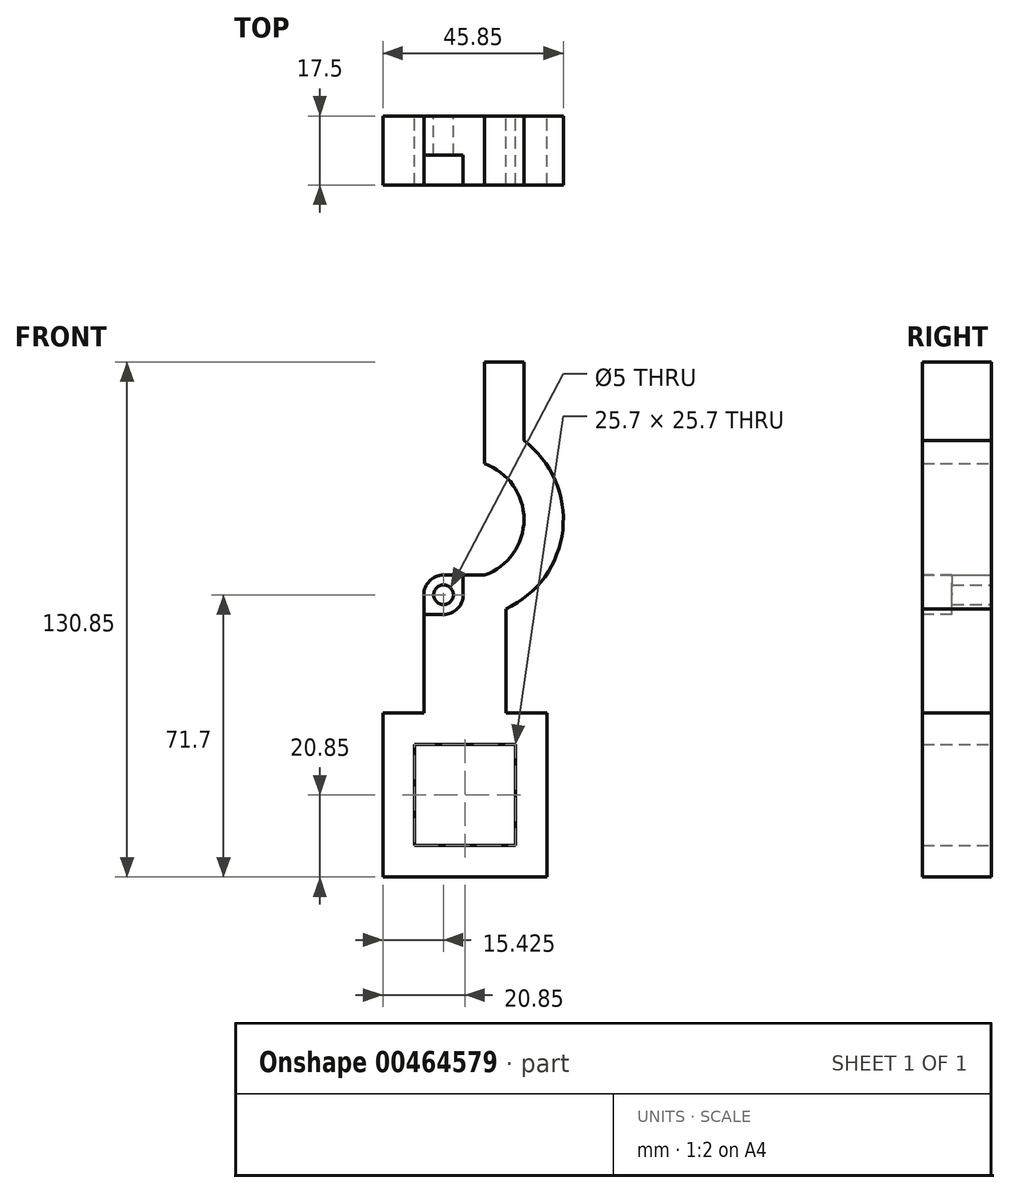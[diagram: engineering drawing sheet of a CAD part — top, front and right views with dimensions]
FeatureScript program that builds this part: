
annotation { "Feature Type Name" : "Feature", "Feature Type Description" : "" }
export const myFeature = defineFeature(function(context is Context, id is Id, definition is map)
    precondition{}
    {
        {
            var Q0;
            Q0=qCreatedBy(makeId("Front.planeOp"),FACE);
            var sketch = newSketch(context, id + "F0", { "sketchPlane" : qUnion([Q0])});
            skLineSegment(sketch, "E0", {"start": v(0, 0) * mm, "end": v(0, 12.85) * mm, "construction": true});
            skLineSegment(sketch, "E1", {"start": v(0, 12.85) * mm, "end": v(12.85, 12.85) * mm});
            skLineSegment(sketch, "E2", {"start": v(12.85, 12.85) * mm, "end": v(12.85, 0) * mm});
            skLineSegment(sketch, "E3", {"start": v(12.85, 0) * mm, "end": v(0, 0) * mm, "construction": true});
            skLineSegment(sketch, "E4", {"start": v(12.85, 0) * mm, "end": v(12.85, -12.85) * mm});
            skLineSegment(sketch, "E5", {"start": v(12.85, -12.85) * mm, "end": v(0, -12.85) * mm});
            skLineSegment(sketch, "E6", {"start": v(0, -12.85) * mm, "end": v(0, 0) * mm, "construction": true});
            skLineSegment(sketch, "E7", {"start": v(0, 0) * mm, "end": v(-12.85, 0) * mm, "construction": true});
            skLineSegment(sketch, "E8", {"start": v(-12.85, 0) * mm, "end": v(-12.85, 12.85) * mm});
            skLineSegment(sketch, "E9", {"start": v(-12.85, 12.85) * mm, "end": v(0, 12.85) * mm});
            skLineSegment(sketch, "E10", {"start": v(-12.85, 0) * mm, "end": v(-12.85, -12.85) * mm});
            skLineSegment(sketch, "E11", {"start": v(-12.85, -12.85) * mm, "end": v(0, -12.85) * mm});
            skLineSegment(sketch, "E12", {"start": v(-12.85, 0) * mm, "end": v(-20.85, 0) * mm, "construction": true});
            skLineSegment(sketch, "E13", {"start": v(-20.85, 0) * mm, "end": v(-20.85, -20.85) * mm});
            skLineSegment(sketch, "E14", {"start": v(20.85, -20.85) * mm, "end": v(20.85, 0) * mm});
            skLineSegment(sketch, "E15", {"start": v(20.85, 0) * mm, "end": v(12.85, 0) * mm, "construction": true});
            skLineSegment(sketch, "E16", {"start": v(20.85, 0) * mm, "end": v(20.85, 20.85) * mm});
            skLineSegment(sketch, "E17", {"start": v(20.85, 20.85) * mm, "end": v(10.43, 20.85) * mm});
            skLineSegment(sketch, "E18", {"start": v(-20.85, 20.85) * mm, "end": v(-20.85, 0) * mm});
            skLineSegment(sketch, "E19", {"start": v(0, 20.85) * mm, "end": v(0, 12.85) * mm, "construction": true});
            skLineSegment(sketch, "E20", {"start": v(-20.85, -20.85) * mm, "end": v(0, -20.85) * mm});
            skLineSegment(sketch, "E21", {"start": v(0, -20.85) * mm, "end": v(20.85, -20.85) * mm});
            skLineSegment(sketch, "E22", {"start": v(0, -12.85) * mm, "end": v(0, -20.85) * mm, "construction": true});
            skLineSegment(sketch, "E23", {"start": v(10.43, 20.85) * mm, "end": v(10.43, 47.28) * mm});
            skLineSegment(sketch, "E24", {"start": v(-10.43, 20.85) * mm, "end": v(-10.43, 55.85) * mm});
            skLineSegment(sketch, "E25", {"start": v(-10.43, 55.85) * mm, "end": v(4.98, 55.85) * mm});
            skArc(sketch, "E26", {"start": v(10.43, 47.28) * mm, "mid": v(24.86, 67.34) * mm, "end": v(15, 90) * mm});
            skArc(sketch, "E27", {"start": v(4.98, 55.85) * mm, "mid": v(15, 69.99) * mm, "end": v(5, 84.14) * mm});
            skLineSegment(sketch, "E28", {"start": v(0, 70) * mm, "end": v(0, 110) * mm, "construction": true});
            skLineSegment(sketch, "E29", {"start": v(0, 110) * mm, "end": v(5, 110) * mm, "construction": true});
            skLineSegment(sketch, "E30", {"start": v(5, 110) * mm, "end": v(5, 84.14) * mm});
            skLineSegment(sketch, "E31", {"start": v(15, 90) * mm, "end": v(15, 110) * mm});
            skLineSegment(sketch, "E32", {"start": v(15, 110) * mm, "end": v(5, 110) * mm});
            skLineSegment(sketch, "E33", {"start": v(0, 110) * mm, "end": v(-5, 110) * mm, "construction": true});
            skLineSegment(sketch, "E34", {"start": v(-5.43, 55.85) * mm, "end": v(-5.43, 50.85) * mm, "construction": true});
            skLineSegment(sketch, "E35", {"start": v(-5.42, 50.85) * mm, "end": v(-10.43, 50.85) * mm, "construction": true});
            skCircle(sketch, "E36", {"center": v(-5.43, 50.85) * mm, "radius": 2.5 * mm});
            skPoint(sketch, "E37.orphan", {"position": v(10.43, 55.85) * mm});
            skLineSegment(sketch, "E38", {"start": v(-20.85, 20.85) * mm, "end": v(-10.43, 20.85) * mm});
            skSolve(sketch);
        }
        {
            var Q0;
            Q0 = qSketchRegion(id + "F0", true);
            extrude(context, id + "F1", {"entities" : qUnion([Q0]), "depth" : 15 * mm});
        }
        {
            var Q0;
            Q0=makeQuery(id+"F1.opExtrude","SWEPT_EDGE",EDGE,{"disambiguationData":[OSD([sQuery(id+"F0.wireOp",EDGE,"E24"),sQuery(id+"F0.wireOp",EDGE,"E25")])]});
            fillet(context, id + "F2", {"entities" : qUnion([Q0]), "radius" : 5 * mm, "tangentPropagation" : true, "allowEdgeOverflow" : false});
        }
        {
            var Q0;
            Q0=makeQuery(id+"F1.opExtrude","CAP_FACE",FACE,{"disambiguationData":[OSD([sQuery(id+"F0.wireOp",EDGE,"E1"),sQuery(id+"F0.wireOp",EDGE,"E2"),sQuery(id+"F0.wireOp",EDGE,"E4"),sQuery(id+"F0.wireOp",EDGE,"E5"),sQuery(id+"F0.wireOp",EDGE,"E8"),sQuery(id+"F0.wireOp",EDGE,"E9"),sQuery(id+"F0.wireOp",EDGE,"E10"),sQuery(id+"F0.wireOp",EDGE,"E11"),sQuery(id+"F0.wireOp",EDGE,"E13"),sQuery(id+"F0.wireOp",EDGE,"E14"),sQuery(id+"F0.wireOp",EDGE,"E16"),sQuery(id+"F0.wireOp",EDGE,"E17"),sQuery(id+"F0.wireOp",EDGE,"E18"),sQuery(id+"F0.wireOp",EDGE,"E20"),sQuery(id+"F0.wireOp",EDGE,"E21"),sQuery(id+"F0.wireOp",EDGE,"E23"),sQuery(id+"F0.wireOp",EDGE,"E24"),sQuery(id+"F0.wireOp",EDGE,"E25"),sQuery(id+"F0.wireOp",EDGE,"E26"),sQuery(id+"F0.wireOp",EDGE,"E27"),sQuery(id+"F0.wireOp",EDGE,"E30"),sQuery(id+"F0.wireOp",EDGE,"E31"),sQuery(id+"F0.wireOp",EDGE,"E32"),sQuery(id+"F0.wireOp",EDGE,"E36"),sQuery(id+"F0.wireOp",EDGE,"E38")])],"isStart":false});
            var sketch = newSketch(context, id + "F3", { "sketchPlane" : qUnion([Q0])});
            skArc(sketch, "E39", {"start": v(-5.43, 55.85) * mm, "mid": v(-8.96, 54.39) * mm, "end": v(-10.43, 50.85) * mm});
            skLineSegment(sketch, "E40", {"start": v(-5.43, 50.85) * mm, "end": v(-0.43, 50.85) * mm, "construction": true});
            skLineSegment(sketch, "E41", {"start": v(-0.43, 50.85) * mm, "end": v(-0.43, 55.85) * mm});
            skLineSegment(sketch, "E42", {"start": v(-5.43, 50.85) * mm, "end": v(-5.43, 45.85) * mm, "construction": true});
            skLineSegment(sketch, "E43", {"start": v(-5.43, 50.85) * mm, "end": v(-10.43, 50.85) * mm, "construction": true});
            skLineSegment(sketch, "E44", {"start": v(-10.43, 50.85) * mm, "end": v(-10.43, 45.85) * mm});
            skLineSegment(sketch, "E45", {"start": v(-10.43, 45.85) * mm, "end": v(-5.43, 45.85) * mm});
            skLineSegment(sketch, "E46", {"start": v(-5.43, 50.85) * mm, "end": v(-5.43, 55.85) * mm, "construction": true});
            skLineSegment(sketch, "E47", {"start": v(-5.43, 55.85) * mm, "end": v(-0.43, 55.85) * mm});
            skArc(sketch, "E48.trimOffspring", {"start": v(-5.43, 45.85) * mm, "mid": v(-1.89, 47.31) * mm, "end": v(-0.43, 50.85) * mm});
            skSolve(sketch);
        }
        {
            var Q0;
            Q0 = qSketchRegion(id + "F3", true);
            extrude(context, id + "F4", {"entities" : qUnion([Q0]), "operationType" : NewBodyOperationType.REMOVE, "oppositeDirection" : true, "depth" : 5 * mm});
        }
        {
            var Q0;
            Q0=makeQuery(id+"F1.opExtrude","CAP_FACE",FACE,{"disambiguationData":[OSD([sQuery(id+"F0.wireOp",EDGE,"E1"),sQuery(id+"F0.wireOp",EDGE,"E2"),sQuery(id+"F0.wireOp",EDGE,"E4"),sQuery(id+"F0.wireOp",EDGE,"E5"),sQuery(id+"F0.wireOp",EDGE,"E8"),sQuery(id+"F0.wireOp",EDGE,"E9"),sQuery(id+"F0.wireOp",EDGE,"E10"),sQuery(id+"F0.wireOp",EDGE,"E11"),sQuery(id+"F0.wireOp",EDGE,"E13"),sQuery(id+"F0.wireOp",EDGE,"E14"),sQuery(id+"F0.wireOp",EDGE,"E16"),sQuery(id+"F0.wireOp",EDGE,"E17"),sQuery(id+"F0.wireOp",EDGE,"E18"),sQuery(id+"F0.wireOp",EDGE,"E20"),sQuery(id+"F0.wireOp",EDGE,"E21"),sQuery(id+"F0.wireOp",EDGE,"E23"),sQuery(id+"F0.wireOp",EDGE,"E24"),sQuery(id+"F0.wireOp",EDGE,"E25"),sQuery(id+"F0.wireOp",EDGE,"E26"),sQuery(id+"F0.wireOp",EDGE,"E27"),sQuery(id+"F0.wireOp",EDGE,"E30"),sQuery(id+"F0.wireOp",EDGE,"E31"),sQuery(id+"F0.wireOp",EDGE,"E32"),sQuery(id+"F0.wireOp",EDGE,"E36"),sQuery(id+"F0.wireOp",EDGE,"E38")])],"isStart":false});
            extrude(context, id + "F5", {"entities" : qUnion([Q0]), "operationType" : NewBodyOperationType.ADD, "depth" : 2.5 * mm});
        }
    });
